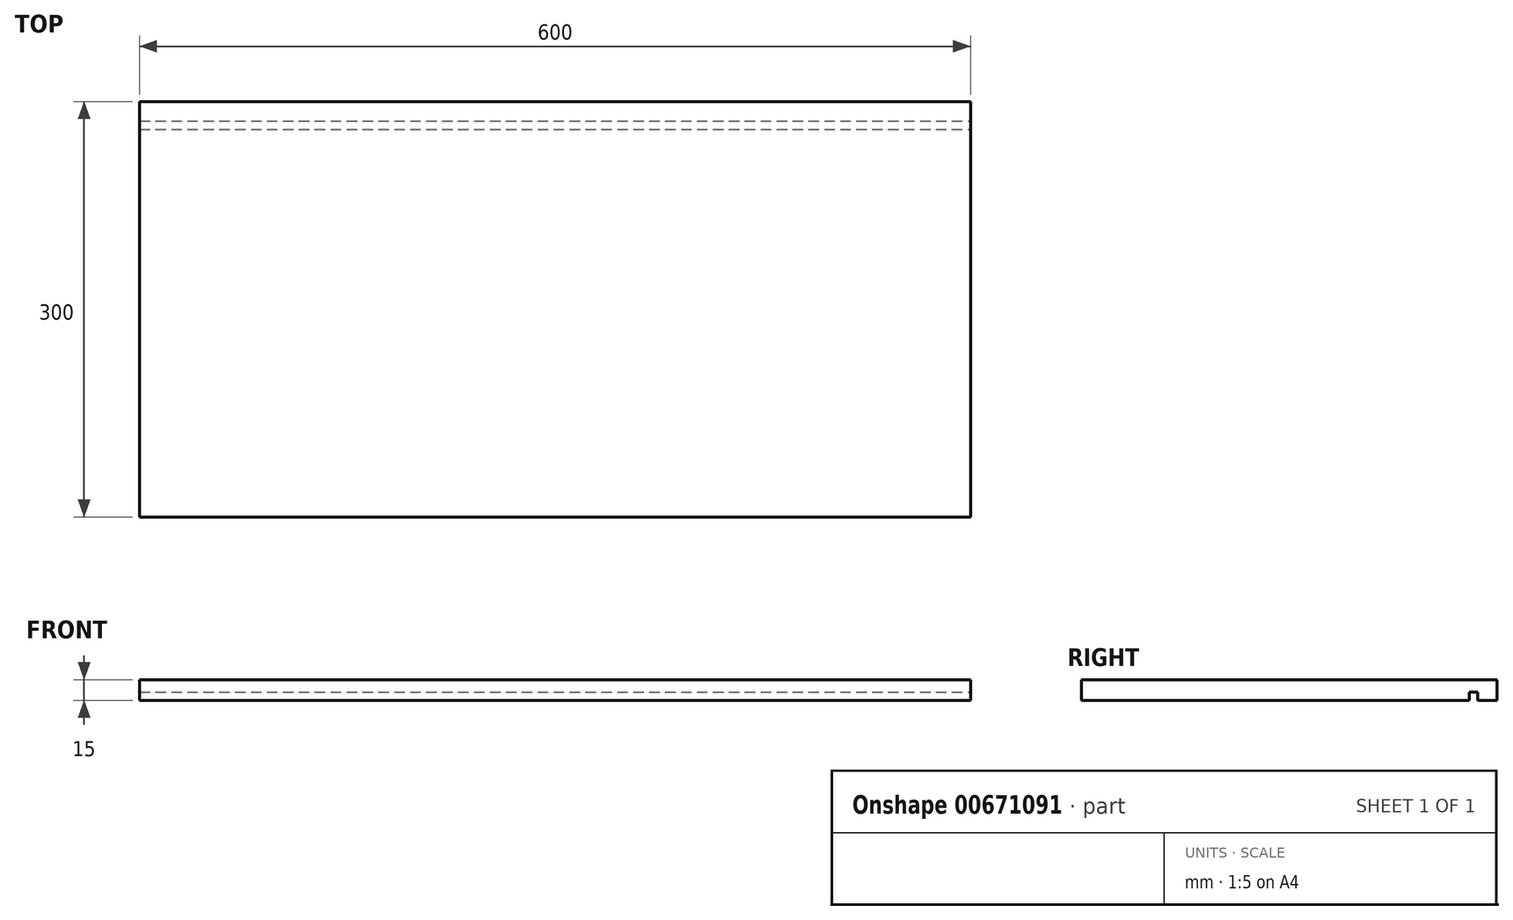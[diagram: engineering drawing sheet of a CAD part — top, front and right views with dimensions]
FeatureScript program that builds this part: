
annotation { "Feature Type Name" : "Feature", "Feature Type Description" : "" }
export const myFeature = defineFeature(function(context is Context, id is Id, definition is map)
    precondition{}
    {
        {
            var Q0;
            Q0=qCreatedBy(makeId("Top.planeOp"),FACE);
            var sketch = newSketch(context, id + "F0", { "sketchPlane" : qUnion([Q0])});
            skLineSegment(sketch, "E0.bottom", {"start": v(0, 0) * mm, "end": v(600, 0) * mm});
            skLineSegment(sketch, "E0.top", {"start": v(0, -300) * mm, "end": v(600, -300) * mm});
            skLineSegment(sketch, "E0.left", {"start": v(0, 0) * mm, "end": v(0, -300) * mm});
            skLineSegment(sketch, "E0.right", {"start": v(600, 0) * mm, "end": v(600, -300) * mm});
            skSolve(sketch);
        }
        {
            var Q0;
            Q0=makeQuery(id+"F0.imprint","IMPRINT",FACE,{"disambiguationData":[TD([[makeQuery(id+"F0.imprint","IMPRINT",EDGE,{"derivedFrom":sQuery(id+"F0.wireOp",EDGE,"E0.bottom")}),-1.0]])]});
            extrude(context, id + "F1", {"entities" : qUnion([Q0]), "depth" : 15 * mm, "offsetDistance" : 25 * mm});
        }
        {
            var Q0;
            Q0=makeQuery(id+"F1.opExtrude","SWEPT_FACE",FACE,{"disambiguationData":[OSD([sQuery(id+"F0.wireOp",EDGE,"E0.right")])]});
            var sketch = newSketch(context, id + "F2", { "sketchPlane" : qUnion([Q0])});
            skLineSegment(sketch, "E1.bottom", {"start": v(-20, 6) * mm, "end": v(-14, 6) * mm});
            skLineSegment(sketch, "E1.top", {"start": v(-20, 0) * mm, "end": v(-14, 0) * mm});
            skLineSegment(sketch, "E1.left", {"start": v(-20, 6) * mm, "end": v(-20, 0) * mm});
            skLineSegment(sketch, "E1.right", {"start": v(-14, 6) * mm, "end": v(-14, 0) * mm});
            skSolve(sketch);
        }
        {
            var Q0;
            Q0=makeQuery(id+"F2.imprint","IMPRINT",FACE,{"disambiguationData":[TD([[makeQuery(id+"F2.imprint","IMPRINT",EDGE,{"derivedFrom":sQuery(id+"F2.wireOp",EDGE,"E1.bottom")}),-1.0]])]});
            extrude(context, id + "F3", {"entities" : qUnion([Q0]), "operationType" : NewBodyOperationType.REMOVE, "oppositeDirection" : true, "depth" : 600 * mm, "offsetDistance" : 25 * mm});
        }
    });
